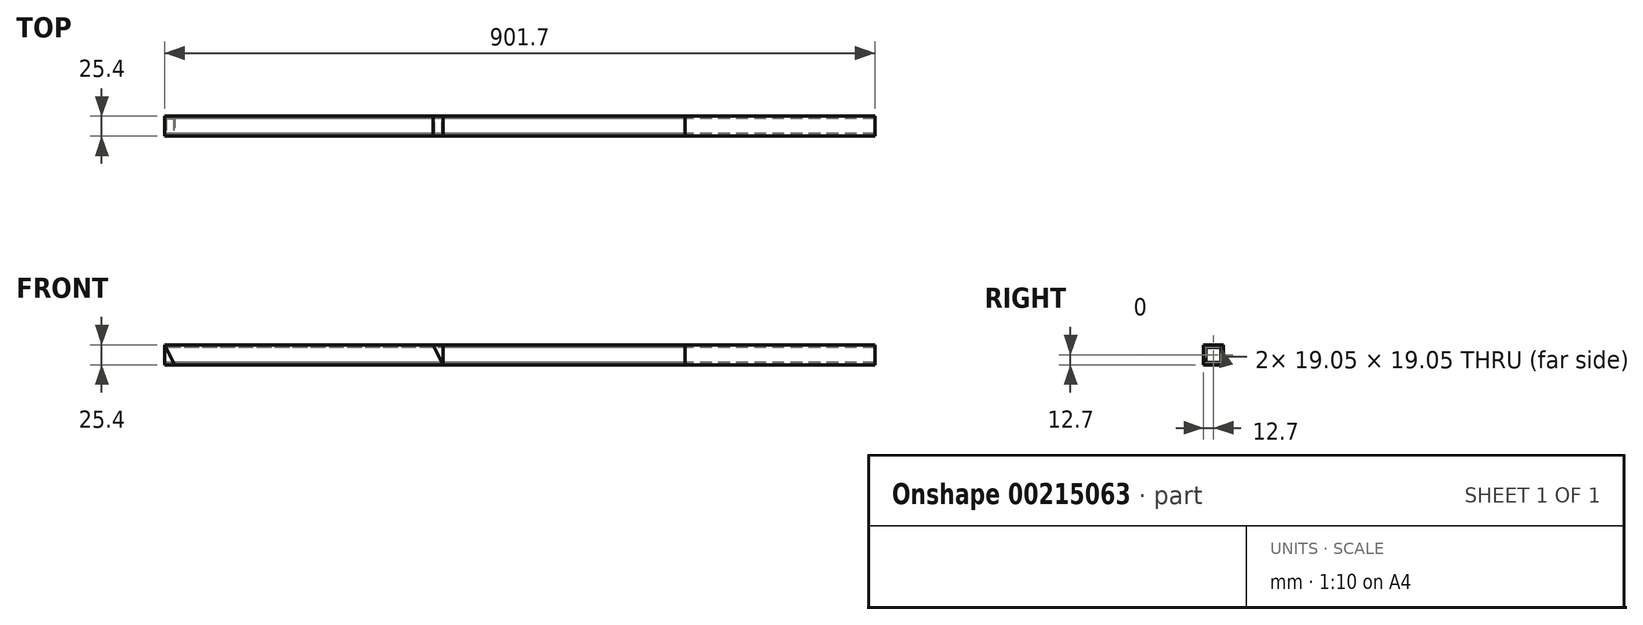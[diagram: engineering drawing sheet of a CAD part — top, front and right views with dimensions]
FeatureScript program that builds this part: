
annotation { "Feature Type Name" : "Feature", "Feature Type Description" : "" }
export const myFeature = defineFeature(function(context is Context, id is Id, definition is map)
    precondition{}
    {
        {
            var Q0;
            Q0=qCreatedBy(makeId("Right.planeOp"),FACE);
            var sketch = newSketch(context, id + "F0", { "sketchPlane" : qUnion([Q0])});
            skLineSegment(sketch, "E0.bottom", {"start": v(0, 0) * mm, "end": v(25.4, 0) * mm});
            skLineSegment(sketch, "E0.top", {"start": v(0, 25.4) * mm, "end": v(25.4, 25.4) * mm});
            skLineSegment(sketch, "E0.left", {"start": v(0, 0) * mm, "end": v(0, 25.4) * mm});
            skLineSegment(sketch, "E0.right", {"start": v(25.4, 0) * mm, "end": v(25.4, 25.4) * mm});
            skLineSegment(sketch, "E1.bottom", {"start": v(3.18, 3.17) * mm, "end": v(22.22, 3.17) * mm});
            skLineSegment(sketch, "E1.top", {"start": v(3.17, 22.23) * mm, "end": v(22.22, 22.23) * mm});
            skLineSegment(sketch, "E1.left", {"start": v(3.18, 3.18) * mm, "end": v(3.17, 22.23) * mm});
            skLineSegment(sketch, "E1.right", {"start": v(22.22, 3.18) * mm, "end": v(22.22, 22.23) * mm});
            skSolve(sketch);
        }
        {
            var Q0;
            Q0 = qSketchRegion(id + "F0", true);
            extrude(context, id + "F1", {"entities" : qUnion([Q0]), "depth" : 901.7 * mm, "offsetDistance" : 25.4 * mm});
        }
        {
            var Q0;
            Q0=qCreatedBy(makeId("Right.planeOp"),FACE);
            var sketch = newSketch(context, id + "F2", { "sketchPlane" : qUnion([Q0])});
            skLineSegment(sketch, "E2.bottom", {"start": v(0, 0) * mm, "end": v(25.4, 0) * mm});
            skLineSegment(sketch, "E2.top", {"start": v(0, 25.4) * mm, "end": v(25.4, 25.4) * mm});
            skLineSegment(sketch, "E2.left", {"start": v(0, 0) * mm, "end": v(0, 25.4) * mm});
            skLineSegment(sketch, "E2.right", {"start": v(25.4, 0) * mm, "end": v(25.4, 25.4) * mm});
            skLineSegment(sketch, "E3.bottom", {"start": v(3.18, 3.18) * mm, "end": v(22.23, 3.18) * mm});
            skLineSegment(sketch, "E3.top", {"start": v(3.17, 22.22) * mm, "end": v(22.22, 22.22) * mm});
            skLineSegment(sketch, "E3.left", {"start": v(3.17, 3.18) * mm, "end": v(3.17, 22.22) * mm});
            skLineSegment(sketch, "E3.right", {"start": v(22.23, 3.18) * mm, "end": v(22.22, 22.22) * mm});
            skSolve(sketch);
        }
        {
            var Q0;
            Q0 = qSketchRegion(id + "F2", true);
            extrude(context, id + "F3", {"entities" : qUnion([Q0]), "depth" : 353.4 * mm, "offsetDistance" : 25.4 * mm});
        }
        {
            var Q0;
            Q0=makeQuery(id+"F3.opExtrude","SWEPT_FACE",FACE,{"disambiguationData":[OSD([sQuery(id+"F2.wireOp",EDGE,"E2.left")])]});
            var sketch = newSketch(context, id + "F4", { "sketchPlane" : qUnion([Q0])});
            skLineSegment(sketch, "E4", {"start": v(353.4, 0) * mm, "end": v(340.7, 25.4) * mm});
            skLineSegment(sketch, "E5", {"start": v(340.7, 25.4) * mm, "end": v(353.4, 25.4) * mm});
            skLineSegment(sketch, "E6", {"start": v(353.4, 25.4) * mm, "end": v(353.4, 0) * mm});
            skLineSegment(sketch, "E7", {"start": v(0, 25.4) * mm, "end": v(12.69, 0) * mm});
            skLineSegment(sketch, "E8", {"start": v(12.69, 0) * mm, "end": v(0, 0) * mm});
            skLineSegment(sketch, "E9", {"start": v(0, 0) * mm, "end": v(0, 25.4) * mm});
            skSolve(sketch);
        }
        {
            var Q0;
            Q0 = qSketchRegion(id + "F4", true);
            var Q1;
            Q1=makeQuery(id+"F3.opExtrude","SWEPT_FACE",FACE,{"disambiguationData":[OSD([sQuery(id+"F2.wireOp",EDGE,"E2.right")])]});
            extrude(context, id + "F5", {"entities" : qUnion([Q0]), "operationType" : NewBodyOperationType.REMOVE, "endBound" : BoundingType.UP_TO_SURFACE, "oppositeDirection" : true, "depth" : 25.4 * mm, "endBoundEntityFace" : qUnion([Q1]), "offsetDistance" : 25.4 * mm});
        }
        {
            var Q0;
            Q0=qCreatedBy(makeId("Right.planeOp"),FACE);
            var sketch = newSketch(context, id + "F6", { "sketchPlane" : qUnion([Q0])});
            skLineSegment(sketch, "E10.bottom", {"start": v(0, 0) * mm, "end": v(25.4, 0) * mm});
            skLineSegment(sketch, "E10.top", {"start": v(0, 25.4) * mm, "end": v(25.4, 25.4) * mm});
            skLineSegment(sketch, "E10.left", {"start": v(0, 0) * mm, "end": v(0, 25.4) * mm});
            skLineSegment(sketch, "E10.right", {"start": v(25.4, 0) * mm, "end": v(25.4, 25.4) * mm});
            skLineSegment(sketch, "E11.bottom", {"start": v(3.18, 3.18) * mm, "end": v(22.23, 3.18) * mm});
            skLineSegment(sketch, "E11.top", {"start": v(3.17, 22.22) * mm, "end": v(22.22, 22.22) * mm});
            skLineSegment(sketch, "E11.left", {"start": v(3.17, 3.18) * mm, "end": v(3.17, 22.22) * mm});
            skLineSegment(sketch, "E11.right", {"start": v(22.23, 3.18) * mm, "end": v(22.22, 22.22) * mm});
            skSolve(sketch);
        }
        {
            var Q0;
            Q0 = qSketchRegion(id + "F6", true);
            extrude(context, id + "F7", {"entities" : qUnion([Q0]), "depth" : 660.4 * mm, "offsetDistance" : 25.4 * mm});
        }
    });
